FCSTD DOCUMENT  (FreeCAD 1.0R39109 (Git))
Label: 05_assembly_u_1-3
License: All rights reserved
LicenseURL: http://en.wikipedia.org/wiki/All_rights_reserved
objects: App::Link×60, App::FeaturePython×28, Assembly::AssemblyLink×10, TechDraw::DrawProjGroupItem×2, Spreadsheet::Sheet×1, TechDraw::DrawSVGTemplate×1, Assembly::JointGroup×1, Assembly::AssemblyObject×1, TechDraw::DrawProjGroup×1, TechDraw::DrawViewDimension×1, TechDraw::DrawPage×1
note: 2 computed .brp shape members not serialized (recipe doc carries the construction recipe); baked Part::Feature solids carry a one-line shape summary decoded from their .brp
EXTERNAL_REF file=10_assembly_u-shape.FCStd obj=Assembly
EXTERNAL_REF file=11_foot.FCStd obj=Body
EXTERNAL_REF file=12_cross_beam.FCStd obj=Body
EXTERNAL_REF file=10_assembly_u-shape.FCStd obj=Body
EXTERNAL_REF file=10_assembly_u-shape.FCStd obj=Body001
EXTERNAL_REF file=10_assembly_u-shape.FCStd obj=Body002

FEATURE [App::Link] Body
  LinkedObject = -> <external 11_foot.FCStd>#Body
FEATURE [App::Link] Body001
  LinkPlacement = pos=(-1.033e-13,1034,2.296e-13) rot=(0,0,1;3.14159rad)
  LinkedObject = -> <external 11_foot.FCStd>#Body
  Placement = pos=(-1.033e-13,1034,2.296e-13) rot=(0,0,1;3.14159rad)
FEATURE [App::Link] Body002
  LinkPlacement = pos=(-1.129e-13,-18,18) rot=(-1,0,0;1.5708rad)
  LinkedObject = -> <external 12_cross_beam.FCStd>#Body
  Placement = pos=(-1.129e-13,-18,18) rot=(-1,0,0;1.5708rad)
FEATURE [App::Link] Body003
  LinkedObject = -> <external 11_foot.FCStd>#Body
FEATURE [App::Link] Body004
  LinkPlacement = pos=(-1.033e-13,1034,2.296e-13) rot=(0,0,1;3.14159rad)
  LinkedObject = -> <external 11_foot.FCStd>#Body
  Placement = pos=(-1.033e-13,1034,2.296e-13) rot=(0,0,1;3.14159rad)
FEATURE [App::Link] Body005
  LinkPlacement = pos=(-1.129e-13,-18,18) rot=(-1,0,0;1.5708rad)
  LinkedObject = -> <external 12_cross_beam.FCStd>#Body
  Placement = pos=(-1.129e-13,-18,18) rot=(-1,0,0;1.5708rad)
FEATURE [Spreadsheet::Sheet] Spreadsheet
  cells = A2='Distanz; B2(distance)=36
FEATURE [App::FeaturePython] Joint  label="Distance"  # Assembly joint (typed FeaturePython)
  Activated = true
  AngleMax = 0
  AngleMin = 0
  Detach1 = false
  Detach2 = false
  Distance = 0
  Distance2 = 0
  EnableAngleMax = false
  EnableAngleMin = false
  EnableLengthMax = false
  EnableLengthMin = false
  JointType = 5 (Distance)
  LengthMax = 0
  LengthMin = 0
  Placement1 = pos=(3.8e-15,-17,122.081) rot=(1,0,0;4.71239rad)
  Placement2 = pos=(3.8e-15,-17,122.081) rot=(1,0,0;4.71239rad)
  Reference1 = -> Assembly [Assembly001.Body001.Face3,Assembly001.Body001.Vertex13]
  Reference2 = -> Assembly [Assembly002.Body004.Face3,Assembly002.Body004.Vertex12]
FEATURE [App::FeaturePython] Joint001  label="Distance001"  # Assembly joint (typed FeaturePython)
  Activated = true
  AngleMax = 0
  AngleMin = 0
  Detach1 = false
  Detach2 = false
  Distance = 0
  Distance2 = 0
  EnableAngleMax = false
  EnableAngleMin = false
  EnableLengthMax = false
  EnableLengthMin = false
  JointType = 5 (Distance)
  LengthMax = 0
  LengthMin = 0
  Placement1 = pos=(-1e-15,17,535) rot=(0,-0.707107,0.707107;3.14159rad)
  Placement2 = pos=(-1e-15,17,535) rot=(0,-0.707107,0.707107;3.14159rad)
  Reference1 = -> Assembly [Assembly001.Body002.Face5,Assembly001.Body002.Vertex23]
  Reference2 = -> Assembly [Assembly002.Body005.Face5,Assembly002.Body005.Vertex23]
FEATURE [App::FeaturePython] Joint002  label="Distance002"  # Assembly joint (typed FeaturePython)
  Activated = true
  AngleMax = 0
  AngleMin = 0
  Detach1 = false
  Detach2 = false
  Distance = -36
  Distance2 = 0
  EnableAngleMax = false
  EnableAngleMin = false
  EnableLengthMax = false
  EnableLengthMin = false
  JointType = 5 (Distance)
  LengthMax = 0
  LengthMin = 0
  Placement1 = pos=(-17,0,117.5) rot=(-0.57735,0.57735,-0.57735;2.0944rad)
  Placement2 = pos=(17,0,117.5) rot=(0.57735,0.57735,-0.57735;4.18879rad)
  Reference1 = -> Assembly [Assembly001.Body001.Face1,Assembly001.Body001.Face1]
  Reference2 = -> Assembly [Assembly002.Body004.Face10,Assembly002.Body004.Vertex5]
  expr: Distance = -Spreadsheet.distance
FEATURE [App::Link] Body006
  LinkedObject = -> <external 11_foot.FCStd>#Body
FEATURE [App::Link] Body007
  LinkPlacement = pos=(-1.033e-13,1034,2.296e-13) rot=(0,0,1;3.14159rad)
  LinkedObject = -> <external 11_foot.FCStd>#Body
  Placement = pos=(-1.033e-13,1034,2.296e-13) rot=(0,0,1;3.14159rad)
FEATURE [App::Link] Body008
  LinkPlacement = pos=(-1.129e-13,-18,18) rot=(-1,0,0;1.5708rad)
  LinkedObject = -> <external 12_cross_beam.FCStd>#Body
  Placement = pos=(-1.129e-13,-18,18) rot=(-1,0,0;1.5708rad)
FEATURE [App::FeaturePython] Joint003  label="Distance003"  # Assembly joint (typed FeaturePython)
  Activated = true
  AngleMax = 0
  AngleMin = 0
  Detach1 = false
  Detach2 = false
  Distance = 0
  Distance2 = 0
  EnableAngleMax = false
  EnableAngleMin = false
  EnableLengthMax = false
  EnableLengthMin = false
  JointType = 5 (Distance)
  LengthMax = 0
  LengthMin = 0
  Placement1 = pos=(3.8e-15,-17,122.081) rot=(1,0,0;4.71239rad)
  Placement2 = pos=(3.8e-15,-17,122.081) rot=(1,0,0;4.71239rad)
  Reference1 = -> Assembly [Assembly003.Body007.Face3,Assembly003.Body007.Vertex12]
  Reference2 = -> Assembly [Assembly002.Body004.Face3,Assembly002.Body004.Vertex13]
FEATURE [App::FeaturePython] Joint004  label="Distance004"  # Assembly joint (typed FeaturePython)
  Activated = true
  AngleMax = 0
  AngleMin = 0
  Detach1 = false
  Detach2 = false
  Distance = 0
  Distance2 = 0
  EnableAngleMax = false
  EnableAngleMin = false
  EnableLengthMax = false
  EnableLengthMin = false
  JointType = 5 (Distance)
  LengthMax = 0
  LengthMin = 0
  Placement1 = pos=(-1e-15,17,535) rot=(0,-0.707107,0.707107;3.14159rad)
  Placement2 = pos=(-1e-15,17,535) rot=(0,-0.707107,0.707107;3.14159rad)
  Reference1 = -> Assembly [Assembly002.Body005.Face5,Assembly002.Body005.Face5]
  Reference2 = -> Assembly [Assembly003.Body008.Face5,Assembly003.Body008.Face5]
FEATURE [App::FeaturePython] Joint005  label="Distance005"  # Assembly joint (typed FeaturePython)
  Activated = true
  AngleMax = 0
  AngleMin = 0
  Detach1 = false
  Detach2 = false
  Distance = -36
  Distance2 = 0
  EnableAngleMax = false
  EnableAngleMin = false
  EnableLengthMax = false
  EnableLengthMin = false
  JointType = 5 (Distance)
  LengthMax = 0
  LengthMin = 0
  Placement1 = pos=(-17,0,117.5) rot=(-0.57735,0.57735,-0.57735;2.0944rad)
  Placement2 = pos=(17,0,117.5) rot=(0.57735,0.57735,-0.57735;4.18879rad)
  Reference1 = -> Assembly [Assembly002.Body004.Face1,Assembly002.Body004.Vertex3]
  Reference2 = -> Assembly [Assembly003.Body007.Face10,Assembly003.Body007.Face10]
  expr: Distance = -Spreadsheet.distance
FEATURE [App::Link] Body009
  LinkedObject = -> <external 11_foot.FCStd>#Body
FEATURE [App::Link] Body010
  LinkPlacement = pos=(-1.033e-13,1034,2.296e-13) rot=(0,0,1;3.14159rad)
  LinkedObject = -> <external 11_foot.FCStd>#Body
  Placement = pos=(-1.033e-13,1034,2.296e-13) rot=(0,0,1;3.14159rad)
FEATURE [App::Link] Body011
  LinkPlacement = pos=(-1.129e-13,-18,18) rot=(-1,0,0;1.5708rad)
  LinkedObject = -> <external 12_cross_beam.FCStd>#Body
  Placement = pos=(-1.129e-13,-18,18) rot=(-1,0,0;1.5708rad)
FEATURE [App::Link] Body012
  LinkedObject = -> <external 11_foot.FCStd>#Body
FEATURE [App::Link] Body013
  LinkPlacement = pos=(-1.033e-13,1034,2.296e-13) rot=(0,0,1;3.14159rad)
  LinkedObject = -> <external 11_foot.FCStd>#Body
  Placement = pos=(-1.033e-13,1034,2.296e-13) rot=(0,0,1;3.14159rad)
FEATURE [App::Link] Body014
  LinkPlacement = pos=(-1.129e-13,-18,18) rot=(-1,0,0;1.5708rad)
  LinkedObject = -> <external 12_cross_beam.FCStd>#Body
  Placement = pos=(-1.129e-13,-18,18) rot=(-1,0,0;1.5708rad)
FEATURE [App::Link] Body015
  LinkedObject = -> <external 11_foot.FCStd>#Body
FEATURE [App::Link] Body016
  LinkPlacement = pos=(-1.033e-13,1034,2.296e-13) rot=(0,0,1;3.14159rad)
  LinkedObject = -> <external 11_foot.FCStd>#Body
  Placement = pos=(-1.033e-13,1034,2.296e-13) rot=(0,0,1;3.14159rad)
FEATURE [App::Link] Body017
  LinkPlacement = pos=(-1.129e-13,-18,18) rot=(-1,0,0;1.5708rad)
  LinkedObject = -> <external 12_cross_beam.FCStd>#Body
  Placement = pos=(-1.129e-13,-18,18) rot=(-1,0,0;1.5708rad)
FEATURE [App::Link] Body018
  LinkedObject = -> <external 11_foot.FCStd>#Body
FEATURE [App::Link] Body019
  LinkPlacement = pos=(-1.033e-13,1034,2.296e-13) rot=(0,0,1;3.14159rad)
  LinkedObject = -> <external 11_foot.FCStd>#Body
  Placement = pos=(-1.033e-13,1034,2.296e-13) rot=(0,0,1;3.14159rad)
FEATURE [App::Link] Body020
  LinkPlacement = pos=(-1.129e-13,-18,18) rot=(-1,0,0;1.5708rad)
  LinkedObject = -> <external 12_cross_beam.FCStd>#Body
  Placement = pos=(-1.129e-13,-18,18) rot=(-1,0,0;1.5708rad)
FEATURE [App::FeaturePython] Joint006  label="Distance006"  # Assembly joint (typed FeaturePython)
  Activated = true
  AngleMax = 0
  AngleMin = 0
  Detach1 = false
  Detach2 = false
  Distance = 0
  Distance2 = 0
  EnableAngleMax = false
  EnableAngleMin = false
  EnableLengthMax = false
  EnableLengthMin = false
  JointType = 5 (Distance)
  LengthMax = 0
  LengthMin = 0
  Placement1 = pos=(3.8e-15,-17,122.081) rot=(1,0,0;4.71239rad)
  Placement2 = pos=(3.8e-15,-17,122.081) rot=(1,0,0;4.71239rad)
  Reference1 = -> Assembly [Assembly004.Body010.Face3,Assembly004.Body010.Vertex12]
  Reference2 = -> Assembly [Assembly003.Body007.Face3,Assembly003.Body007.Face3]
FEATURE [App::FeaturePython] Joint007  label="Distance007"  # Assembly joint (typed FeaturePython)
  Activated = true
  AngleMax = 0
  AngleMin = 0
  Detach1 = false
  Detach2 = false
  Distance = 0
  Distance2 = 0
  EnableAngleMax = false
  EnableAngleMin = false
  EnableLengthMax = false
  EnableLengthMin = false
  JointType = 5 (Distance)
  LengthMax = 0
  LengthMin = 0
  Placement1 = pos=(-1e-15,17,535) rot=(0,-0.707107,0.707107;3.14159rad)
  Placement2 = pos=(-1e-15,17,535) rot=(0,-0.707107,0.707107;3.14159rad)
  Reference1 = -> Assembly [Assembly004.Body011.Face5,Assembly004.Body011.Vertex23]
  Reference2 = -> Assembly [Assembly003.Body008.Face5,Assembly003.Body008.Vertex4]
FEATURE [App::FeaturePython] Joint008  label="Distance008"  # Assembly joint (typed FeaturePython)
  Activated = true
  AngleMax = 0
  AngleMin = 0
  Detach1 = false
  Detach2 = false
  Distance = -36
  Distance2 = 0
  EnableAngleMax = false
  EnableAngleMin = false
  EnableLengthMax = false
  EnableLengthMin = false
  JointType = 5 (Distance)
  LengthMax = 0
  LengthMin = 0
  Placement1 = pos=(-17,0,117.5) rot=(-0.57735,0.57735,-0.57735;2.0944rad)
  Placement2 = pos=(17,0,117.5) rot=(0.57735,0.57735,-0.57735;4.18879rad)
  Reference1 = -> Assembly [Assembly003.Body007.Face1,Assembly003.Body007.Vertex3]
  Reference2 = -> Assembly [Assembly004.Body010.Face10,Assembly004.Body010.Vertex5]
  expr: Distance = -<<Spreadsheet>>.distance
FEATURE [App::FeaturePython] Joint009  label="Distance009"  # Assembly joint (typed FeaturePython)
  Activated = true
  AngleMax = 0
  AngleMin = 0
  Detach1 = false
  Detach2 = false
  Distance = 0
  Distance2 = 0
  EnableAngleMax = false
  EnableAngleMin = false
  EnableLengthMax = false
  EnableLengthMin = false
  JointType = 5 (Distance)
  LengthMax = 0
  LengthMin = 0
  Placement1 = pos=(3.8e-15,-17,122.081) rot=(1,0,0;4.71239rad)
  Placement2 = pos=(3.8e-15,-17,122.081) rot=(1,0,0;4.71239rad)
  Reference1 = -> Assembly [Assembly005.Body013.Face3,Assembly005.Body013.Vertex12]
  Reference2 = -> Assembly [Assembly004.Body010.Face3,Assembly004.Body010.Vertex13]
FEATURE [App::FeaturePython] Joint010  label="Distance010"  # Assembly joint (typed FeaturePython)
  Activated = true
  AngleMax = 0
  AngleMin = 0
  Detach1 = false
  Detach2 = false
  Distance = 0
  Distance2 = 0
  EnableAngleMax = false
  EnableAngleMin = false
  EnableLengthMax = false
  EnableLengthMin = false
  JointType = 5 (Distance)
  LengthMax = 0
  LengthMin = 0
  Placement1 = pos=(-1e-15,17,535) rot=(0,-0.707107,0.707107;3.14159rad)
  Placement2 = pos=(-1e-15,17,535) rot=(0,-0.707107,0.707107;3.14159rad)
  Reference1 = -> Assembly [Assembly005.Body014.Face5,Assembly005.Body014.Vertex16]
  Reference2 = -> Assembly [Assembly004.Body011.Face5,Assembly004.Body011.Face5]
FEATURE [App::FeaturePython] Joint011  label="Distance011"  # Assembly joint (typed FeaturePython)
  Activated = true
  AngleMax = 0
  AngleMin = 0
  Detach1 = false
  Detach2 = false
  Distance = -36
  Distance2 = 0
  EnableAngleMax = false
  EnableAngleMin = false
  EnableLengthMax = false
  EnableLengthMin = false
  JointType = 5 (Distance)
  LengthMax = 0
  LengthMin = 0
  Placement1 = pos=(-17,0,117.5) rot=(-0.57735,0.57735,-0.57735;2.0944rad)
  Placement2 = pos=(17,0,117.5) rot=(0.57735,0.57735,-0.57735;4.18879rad)
  Reference1 = -> Assembly [Assembly004.Body010.Face1,Assembly004.Body010.Face1]
  Reference2 = -> Assembly [Assembly005.Body013.Face10,Assembly005.Body013.Vertex5]
  expr: Distance = -Spreadsheet.distance
FEATURE [App::FeaturePython] Joint012  label="Distance012"  # Assembly joint (typed FeaturePython)
  Activated = true
  AngleMax = 0
  AngleMin = 0
  Detach1 = false
  Detach2 = false
  Distance = 0
  Distance2 = 0
  EnableAngleMax = false
  EnableAngleMin = false
  EnableLengthMax = false
  EnableLengthMin = false
  JointType = 5 (Distance)
  LengthMax = 0
  LengthMin = 0
  Placement1 = pos=(3.8e-15,-17,122.081) rot=(1,0,0;4.71239rad)
  Placement2 = pos=(3.8e-15,-17,122.081) rot=(1,0,0;4.71239rad)
  Reference1 = -> Assembly [Assembly005.Body013.Face3,Assembly005.Body013.Face3]
  Reference2 = -> Assembly [Assembly006.Body016.Face3,Assembly006.Body016.Vertex13]
FEATURE [App::FeaturePython] Joint013  label="Distance013"  # Assembly joint (typed FeaturePython)
  Activated = true
  AngleMax = 0
  AngleMin = 0
  Detach1 = false
  Detach2 = false
  Distance = 0
  Distance2 = 0
  EnableAngleMax = false
  EnableAngleMin = false
  EnableLengthMax = false
  EnableLengthMin = false
  JointType = 5 (Distance)
  LengthMax = 0
  LengthMin = 0
  Placement1 = pos=(-1e-15,17,535) rot=(0,-0.707107,0.707107;3.14159rad)
  Placement2 = pos=(-1e-15,17,535) rot=(0,-0.707107,0.707107;3.14159rad)
  Reference1 = -> Assembly [Assembly006.Body017.Face5,Assembly006.Body017.Vertex23]
  Reference2 = -> Assembly [Assembly005.Body014.Face5,Assembly005.Body014.Vertex16]
FEATURE [App::FeaturePython] Joint014  label="Distance014"  # Assembly joint (typed FeaturePython)
  Activated = true
  AngleMax = 0
  AngleMin = 0
  Detach1 = false
  Detach2 = false
  Distance = -36
  Distance2 = 0
  EnableAngleMax = false
  EnableAngleMin = false
  EnableLengthMax = false
  EnableLengthMin = false
  JointType = 5 (Distance)
  LengthMax = 0
  LengthMin = 0
  Placement1 = pos=(17,0,117.5) rot=(0.57735,0.57735,-0.57735;4.18879rad)
  Placement2 = pos=(-17,0,117.5) rot=(-0.57735,0.57735,-0.57735;2.0944rad)
  Reference1 = -> Assembly [Assembly006.Body016.Face10,Assembly006.Body016.Vertex5]
  Reference2 = -> Assembly [Assembly005.Body013.Face1,Assembly005.Body013.Face1]
  expr: Distance = -Spreadsheet.distance
FEATURE [App::FeaturePython] Joint015  label="Distance015"  # Assembly joint (typed FeaturePython)
  Activated = true
  AngleMax = 0
  AngleMin = 0
  Detach1 = false
  Detach2 = false
  Distance = 0
  Distance2 = 0
  EnableAngleMax = false
  EnableAngleMin = false
  EnableLengthMax = false
  EnableLengthMin = false
  JointType = 5 (Distance)
  LengthMax = 0
  LengthMin = 0
  Placement1 = pos=(3.8e-15,-17,122.081) rot=(1,0,0;4.71239rad)
  Placement2 = pos=(3.8e-15,-17,122.081) rot=(1,0,0;4.71239rad)
  Reference1 = -> Assembly [Assembly007.Body019.Face3,Assembly007.Body019.Vertex12]
  Reference2 = -> Assembly [Assembly006.Body016.Face3,Assembly006.Body016.Face3]
FEATURE [App::FeaturePython] Joint016  label="Distance016"  # Assembly joint (typed FeaturePython)
  Activated = true
  AngleMax = 0
  AngleMin = 0
  Detach1 = false
  Detach2 = false
  Distance = 0
  Distance2 = 0
  EnableAngleMax = false
  EnableAngleMin = false
  EnableLengthMax = false
  EnableLengthMin = false
  JointType = 5 (Distance)
  LengthMax = 0
  LengthMin = 0
  Placement1 = pos=(-1e-15,17,535) rot=(0,-0.707107,0.707107;3.14159rad)
  Placement2 = pos=(-1e-15,17,535) rot=(0,-0.707107,0.707107;3.14159rad)
  Reference1 = -> Assembly [Assembly006.Body017.Face5,Assembly006.Body017.Vertex16]
  Reference2 = -> Assembly [Assembly007.Body020.Face5,Assembly007.Body020.Vertex16]
FEATURE [App::FeaturePython] Joint017  label="Distance017"  # Assembly joint (typed FeaturePython)
  Activated = true
  AngleMax = 0
  AngleMin = 0
  Detach1 = false
  Detach2 = false
  Distance = -36
  Distance2 = 0
  EnableAngleMax = false
  EnableAngleMin = false
  EnableLengthMax = false
  EnableLengthMin = false
  JointType = 5 (Distance)
  LengthMax = 0
  LengthMin = 0
  Placement1 = pos=(-17,0,117.5) rot=(-0.57735,0.57735,-0.57735;2.0944rad)
  Placement2 = pos=(17,0,117.5) rot=(0.57735,0.57735,-0.57735;4.18879rad)
  Reference1 = -> Assembly [Assembly006.Body016.Face1,Assembly006.Body016.Vertex1]
  Reference2 = -> Assembly [Assembly007.Body019.Face10,Assembly007.Body019.Vertex15]
  expr: Distance = -Spreadsheet.distance
FEATURE [TechDraw::DrawSVGTemplate] Template
  EditableTexts = approval_person=B. Hecate; creator=A. Nemesis; date_of_issue=22/06/2025; document_type=Assembly Drawing; general_tolerances=ISO 2768-m; identification_number=DN; language_code=EN; part_material=Stainless steel Mat.No. 1.4301; revision_index=AAA; sheet_number=1 / 1; sheet_scale=1 : 1; title=00_assembly_complete_large_x1
  Height = 297
  Orientation = 1
  Template = C:/Program Files/FreeCAD 1.0/data/Mod/TechDraw/Templates/A3_Landscape_ISO5457_minimal.svg
  Width = 420
FEATURE [App::Link] Body021
  LinkedObject = -> <external 11_foot.FCStd>#Body
FEATURE [App::Link] Body022
  LinkPlacement = pos=(-1.033e-13,1034,2.296e-13) rot=(0,0,1;3.14159rad)
  LinkedObject = -> <external 11_foot.FCStd>#Body
  Placement = pos=(-1.033e-13,1034,2.296e-13) rot=(0,0,1;3.14159rad)
FEATURE [App::Link] Body023
  LinkPlacement = pos=(-1.129e-13,-18,18) rot=(-1,0,0;1.5708rad)
  LinkedObject = -> <external 12_cross_beam.FCStd>#Body
  Placement = pos=(-1.129e-13,-18,18) rot=(-1,0,0;1.5708rad)
FEATURE [App::Link] Body024
  LinkedObject = -> <external 11_foot.FCStd>#Body
FEATURE [App::Link] Body025
  LinkPlacement = pos=(-1.033e-13,1034,2.296e-13) rot=(0,0,1;3.14159rad)
  LinkedObject = -> <external 11_foot.FCStd>#Body
  Placement = pos=(-1.033e-13,1034,2.296e-13) rot=(0,0,1;3.14159rad)
FEATURE [App::Link] Body026
  LinkPlacement = pos=(-1.129e-13,-18,18) rot=(-1,0,0;1.5708rad)
  LinkedObject = -> <external 12_cross_beam.FCStd>#Body
  Placement = pos=(-1.129e-13,-18,18) rot=(-1,0,0;1.5708rad)
FEATURE [App::Link] Body027
  LinkedObject = -> <external 11_foot.FCStd>#Body
FEATURE [App::Link] Body028
  LinkPlacement = pos=(-1.033e-13,1034,2.296e-13) rot=(0,0,1;3.14159rad)
  LinkedObject = -> <external 11_foot.FCStd>#Body
  Placement = pos=(-1.033e-13,1034,2.296e-13) rot=(0,0,1;3.14159rad)
FEATURE [App::Link] Body029
  LinkPlacement = pos=(-1.129e-13,-18,18) rot=(-1,0,0;1.5708rad)
  LinkedObject = -> <external 12_cross_beam.FCStd>#Body
  Placement = pos=(-1.129e-13,-18,18) rot=(-1,0,0;1.5708rad)
FEATURE [App::FeaturePython] Joint018  label="Distance018"  # Assembly joint (typed FeaturePython)
  Activated = true
  AngleMax = 0
  AngleMin = 0
  Detach1 = false
  Detach2 = false
  Distance = 0
  Distance2 = 0
  EnableAngleMax = false
  EnableAngleMin = false
  EnableLengthMax = false
  EnableLengthMin = false
  JointType = 5 (Distance)
  LengthMax = 0
  LengthMin = 0
  Placement1 = pos=(-1e-15,17,535) rot=(0,-0.707107,0.707107;3.14159rad)
  Placement2 = pos=(-1e-15,17,535) rot=(0,-0.707107,0.707107;3.14159rad)
  Reference1 = -> Assembly [Assembly007.Body020.Face5,Assembly007.Body020.Vertex23]
  Reference2 = -> Assembly [Assembly008.Body023.Face5,Assembly008.Body023.Vertex16]
FEATURE [App::FeaturePython] Joint019  label="Distance019"  # Assembly joint (typed FeaturePython)
  Activated = true
  AngleMax = 0
  AngleMin = 0
  Detach1 = false
  Detach2 = false
  Distance = 0
  Distance2 = 0
  EnableAngleMax = false
  EnableAngleMin = false
  EnableLengthMax = false
  EnableLengthMin = false
  JointType = 5 (Distance)
  LengthMax = 0
  LengthMin = 0
  Placement1 = pos=(3.8e-15,-17,122.081) rot=(1,0,0;4.71239rad)
  Placement2 = pos=(3.8e-15,-17,122.081) rot=(1,0,0;4.71239rad)
  Reference1 = -> Assembly [Assembly008.Body022.Face3,Assembly008.Body022.Face3]
  Reference2 = -> Assembly [Assembly007.Body019.Face3,Assembly007.Body019.Vertex13]
FEATURE [App::FeaturePython] Joint020  label="Distance020"  # Assembly joint (typed FeaturePython)
  Activated = true
  AngleMax = 0
  AngleMin = 0
  Detach1 = false
  Detach2 = false
  Distance = -36
  Distance2 = 0
  EnableAngleMax = false
  EnableAngleMin = false
  EnableLengthMax = false
  EnableLengthMin = false
  JointType = 5 (Distance)
  LengthMax = 0
  LengthMin = 0
  Placement1 = pos=(-17,0,117.5) rot=(-0.57735,0.57735,-0.57735;2.0944rad)
  Placement2 = pos=(17,0,117.5) rot=(0.57735,0.57735,-0.57735;4.18879rad)
  Reference1 = -> Assembly [Assembly007.Body019.Face1,Assembly007.Body019.Face1]
  Reference2 = -> Assembly [Assembly008.Body022.Face10,Assembly008.Body022.Vertex5]
  expr: Distance = -Spreadsheet.distance
FEATURE [App::FeaturePython] Joint021  label="Distance021"  # Assembly joint (typed FeaturePython)
  Activated = true
  AngleMax = 0
  AngleMin = 0
  Detach1 = false
  Detach2 = false
  Distance = 0
  Distance2 = 0
  EnableAngleMax = false
  EnableAngleMin = false
  EnableLengthMax = false
  EnableLengthMin = false
  JointType = 5 (Distance)
  LengthMax = 0
  LengthMin = 0
  Placement1 = pos=(3.8e-15,-17,122.081) rot=(1,0,0;4.71239rad)
  Placement2 = pos=(3.8e-15,-17,122.081) rot=(1,0,0;4.71239rad)
  Reference1 = -> Assembly [Assembly009.Body025.Face3,Assembly009.Body025.Vertex13]
  Reference2 = -> Assembly [Assembly008.Body022.Face3,Assembly008.Body022.Vertex13]
FEATURE [App::FeaturePython] Joint022  label="Distance022"  # Assembly joint (typed FeaturePython)
  Activated = true
  AngleMax = 0
  AngleMin = 0
  Detach1 = false
  Detach2 = false
  Distance = 0
  Distance2 = 0
  EnableAngleMax = false
  EnableAngleMin = false
  EnableLengthMax = false
  EnableLengthMin = false
  JointType = 5 (Distance)
  LengthMax = 0
  LengthMin = 0
  Placement1 = pos=(-1e-15,17,535) rot=(0,-0.707107,0.707107;3.14159rad)
  Placement2 = pos=(-1e-15,17,535) rot=(0,-0.707107,0.707107;3.14159rad)
  Reference1 = -> Assembly [Assembly009.Body026.Face5,Assembly009.Body026.Face5]
  Reference2 = -> Assembly [Assembly008.Body023.Face5,Assembly008.Body023.Face5]
FEATURE [App::FeaturePython] Joint023  label="Distance023"  # Assembly joint (typed FeaturePython)
  Activated = true
  AngleMax = 0
  AngleMin = 0
  Detach1 = false
  Detach2 = false
  Distance = -36
  Distance2 = 0
  EnableAngleMax = false
  EnableAngleMin = false
  EnableLengthMax = false
  EnableLengthMin = false
  JointType = 5 (Distance)
  LengthMax = 0
  LengthMin = 0
  Placement1 = pos=(-17,0,117.5) rot=(-0.57735,0.57735,-0.57735;2.0944rad)
  Placement2 = pos=(17,0,117.5) rot=(0.57735,0.57735,-0.57735;4.18879rad)
  Reference1 = -> Assembly [Assembly008.Body022.Face1,Assembly008.Body022.Face1]
  Reference2 = -> Assembly [Assembly009.Body025.Face10,Assembly009.Body025.Vertex5]
  expr: Distance = -Spreadsheet.distance
FEATURE [App::FeaturePython] Joint024  label="Distance024"  # Assembly joint (typed FeaturePython)
  Activated = true
  AngleMax = 0
  AngleMin = 0
  Detach1 = false
  Detach2 = false
  Distance = 0
  Distance2 = 0
  EnableAngleMax = false
  EnableAngleMin = false
  EnableLengthMax = false
  EnableLengthMin = false
  JointType = 5 (Distance)
  LengthMax = 0
  LengthMin = 0
  Placement1 = pos=(3.8e-15,-17,122.081) rot=(1,0,0;4.71239rad)
  Placement2 = pos=(3.8e-15,-17,122.081) rot=(1,0,0;4.71239rad)
  Reference1 = -> Assembly [Assembly009.Body025.Face3,Assembly009.Body025.Vertex12]
  Reference2 = -> Assembly [Assembly010.Body028.Face3,Assembly010.Body028.Face3]
FEATURE [App::FeaturePython] Joint025  label="Distance025"  # Assembly joint (typed FeaturePython)
  Activated = true
  AngleMax = 0
  AngleMin = 0
  Detach1 = false
  Detach2 = false
  Distance = 0
  Distance2 = 0
  EnableAngleMax = false
  EnableAngleMin = false
  EnableLengthMax = false
  EnableLengthMin = false
  JointType = 5 (Distance)
  LengthMax = 0
  LengthMin = 0
  Placement1 = pos=(-1e-15,17,535) rot=(0,-0.707107,0.707107;3.14159rad)
  Placement2 = pos=(-1e-15,17,535) rot=(0,-0.707107,0.707107;3.14159rad)
  Reference1 = -> Assembly [Assembly010.Body029.Face5,Assembly010.Body029.Vertex23]
  Reference2 = -> Assembly [Assembly009.Body026.Face5,Assembly009.Body026.Vertex16]
FEATURE [App::FeaturePython] Joint026  label="Distance026"  # Assembly joint (typed FeaturePython)
  Activated = true
  AngleMax = 0
  AngleMin = 0
  Detach1 = false
  Detach2 = false
  Distance = -36
  Distance2 = 0
  EnableAngleMax = false
  EnableAngleMin = false
  EnableLengthMax = false
  EnableLengthMin = false
  JointType = 5 (Distance)
  LengthMax = 0
  LengthMin = 0
  Placement1 = pos=(-17,0,117.5) rot=(-0.57735,0.57735,-0.57735;2.0944rad)
  Placement2 = pos=(17,-17,117.5) rot=(0,0,1;0rad)
  Reference1 = -> Assembly [Assembly009.Body025.Face1,Assembly009.Body025.Face1]
  Reference2 = -> Assembly [Assembly010.Body028.Edge17,Assembly010.Body028.Vertex15]
  expr: Distance = -Spreadsheet.distance
FEATURE [App::Link] Body030
  LinkedObject = -> <external 10_assembly_u-shape.FCStd>#Body
FEATURE [App::Link] Body031
  LinkPlacement = pos=(1.87e-14,1034,-3.446e-13) rot=(0,0,1;3.14159rad)
  LinkedObject = -> <external 10_assembly_u-shape.FCStd>#Body001
  Placement = pos=(1.87e-14,1034,-3.446e-13) rot=(0,0,1;3.14159rad)
FEATURE [App::Link] Body032
  LinkPlacement = pos=(-2.8e-15,-18,18) rot=(1,0,0;4.71239rad)
  LinkedObject = -> <external 10_assembly_u-shape.FCStd>#Body002
  Placement = pos=(-2.8e-15,-18,18) rot=(1,0,0;4.71239rad)
FEATURE [Assembly::AssemblyLink] Assembly001
  Group = -> [Body,Body001,Body002,Body030,Body031,Body032]
  LinkedObject = -> <external 10_assembly_u-shape.FCStd>#Assembly
  Origin = -> Origin001
  Rigid = true
FEATURE [App::FeaturePython] GroundedJoint  # Assembly grounded joint (typed FeaturePython)
  ObjectToGround = -> Assembly001
FEATURE [Assembly::JointGroup] Joints
  Group = -> [GroundedJoint,Joint,Joint001,Joint002,Joint003,Joint004,Joint005,Joint006,Joint007,Joint008,Joint009,Joint010,Joint011,Joint012,Joint013,Joint014,Joint015,Joint016,Joint017,Joint018,Joint019,Joint020,Joint021,Joint022,Joint023,Joint024,Joint025,Joint026]
FEATURE [App::Link] Body033
  LinkedObject = -> <external 10_assembly_u-shape.FCStd>#Body
FEATURE [App::Link] Body034
  LinkPlacement = pos=(1.87e-14,1034,-3.446e-13) rot=(0,0,1;3.14159rad)
  LinkedObject = -> <external 10_assembly_u-shape.FCStd>#Body001
  Placement = pos=(1.87e-14,1034,-3.446e-13) rot=(0,0,1;3.14159rad)
FEATURE [App::Link] Body035
  LinkPlacement = pos=(-2.8e-15,-18,18) rot=(1,0,0;4.71239rad)
  LinkedObject = -> <external 10_assembly_u-shape.FCStd>#Body002
  Placement = pos=(-2.8e-15,-18,18) rot=(1,0,0;4.71239rad)
FEATURE [Assembly::AssemblyLink] Assembly002
  Group = -> [Body003,Body004,Body005,Body033,Body034,Body035]
  LinkedObject = -> <external 10_assembly_u-shape.FCStd>#Assembly
  Origin = -> Origin002
  Placement = pos=(70,9.23e-14,-1.3e-15) rot=(0,0,1;0rad)
  Rigid = true
FEATURE [App::Link] Body036
  LinkedObject = -> <external 10_assembly_u-shape.FCStd>#Body
FEATURE [App::Link] Body037
  LinkPlacement = pos=(1.87e-14,1034,-3.446e-13) rot=(0,0,1;3.14159rad)
  LinkedObject = -> <external 10_assembly_u-shape.FCStd>#Body001
  Placement = pos=(1.87e-14,1034,-3.446e-13) rot=(0,0,1;3.14159rad)
FEATURE [App::Link] Body038
  LinkPlacement = pos=(-2.8e-15,-18,18) rot=(1,0,0;4.71239rad)
  LinkedObject = -> <external 10_assembly_u-shape.FCStd>#Body002
  Placement = pos=(-2.8e-15,-18,18) rot=(1,0,0;4.71239rad)
FEATURE [Assembly::AssemblyLink] Assembly003
  Group = -> [Body006,Body007,Body008,Body036,Body037,Body038]
  LinkedObject = -> <external 10_assembly_u-shape.FCStd>#Assembly
  Origin = -> Origin003
  Placement = pos=(140,-2.86e-14,2.39e-14) rot=(0,0,1;0rad)
  Rigid = true
FEATURE [App::Link] Body039
  LinkedObject = -> <external 10_assembly_u-shape.FCStd>#Body
FEATURE [App::Link] Body040
  LinkPlacement = pos=(1.87e-14,1034,-3.446e-13) rot=(0,0,1;3.14159rad)
  LinkedObject = -> <external 10_assembly_u-shape.FCStd>#Body001
  Placement = pos=(1.87e-14,1034,-3.446e-13) rot=(0,0,1;3.14159rad)
FEATURE [App::Link] Body041
  LinkPlacement = pos=(-2.8e-15,-18,18) rot=(1,0,0;4.71239rad)
  LinkedObject = -> <external 10_assembly_u-shape.FCStd>#Body002
  Placement = pos=(-2.8e-15,-18,18) rot=(1,0,0;4.71239rad)
FEATURE [Assembly::AssemblyLink] Assembly004
  Group = -> [Body009,Body010,Body011,Body039,Body040,Body041]
  LinkedObject = -> <external 10_assembly_u-shape.FCStd>#Assembly
  Origin = -> Origin004
  Placement = pos=(210,2.578e-13,4.84e-14) rot=(0,0,1;0rad)
  Rigid = true
FEATURE [App::Link] Body042
  LinkedObject = -> <external 10_assembly_u-shape.FCStd>#Body
FEATURE [App::Link] Body043
  LinkPlacement = pos=(1.87e-14,1034,-3.446e-13) rot=(0,0,1;3.14159rad)
  LinkedObject = -> <external 10_assembly_u-shape.FCStd>#Body001
  Placement = pos=(1.87e-14,1034,-3.446e-13) rot=(0,0,1;3.14159rad)
FEATURE [App::Link] Body044
  LinkPlacement = pos=(-2.8e-15,-18,18) rot=(1,0,0;4.71239rad)
  LinkedObject = -> <external 10_assembly_u-shape.FCStd>#Body002
  Placement = pos=(-2.8e-15,-18,18) rot=(1,0,0;4.71239rad)
FEATURE [Assembly::AssemblyLink] Assembly005
  Group = -> [Body012,Body013,Body014,Body042,Body043,Body044]
  LinkedObject = -> <external 10_assembly_u-shape.FCStd>#Assembly
  Origin = -> Origin005
  Placement = pos=(280,1.496e-13,1.001e-13) rot=(0,0,1;0rad)
  Rigid = true
FEATURE [App::Link] Body045
  LinkedObject = -> <external 10_assembly_u-shape.FCStd>#Body
FEATURE [App::Link] Body046
  LinkPlacement = pos=(1.87e-14,1034,-3.446e-13) rot=(0,0,1;3.14159rad)
  LinkedObject = -> <external 10_assembly_u-shape.FCStd>#Body001
  Placement = pos=(1.87e-14,1034,-3.446e-13) rot=(0,0,1;3.14159rad)
FEATURE [App::Link] Body047
  LinkPlacement = pos=(-2.8e-15,-18,18) rot=(1,0,0;4.71239rad)
  LinkedObject = -> <external 10_assembly_u-shape.FCStd>#Body002
  Placement = pos=(-2.8e-15,-18,18) rot=(1,0,0;4.71239rad)
FEATURE [Assembly::AssemblyLink] Assembly006
  Group = -> [Body015,Body016,Body017,Body045,Body046,Body047]
  LinkedObject = -> <external 10_assembly_u-shape.FCStd>#Assembly
  Origin = -> Origin006
  Placement = pos=(350,6.31e-14,1.758e-13) rot=(0,0,1;0rad)
  Rigid = true
FEATURE [App::Link] Body048
  LinkedObject = -> <external 10_assembly_u-shape.FCStd>#Body
FEATURE [App::Link] Body049
  LinkPlacement = pos=(1.87e-14,1034,-3.446e-13) rot=(0,0,1;3.14159rad)
  LinkedObject = -> <external 10_assembly_u-shape.FCStd>#Body001
  Placement = pos=(1.87e-14,1034,-3.446e-13) rot=(0,0,1;3.14159rad)
FEATURE [App::Link] Body050
  LinkPlacement = pos=(-2.8e-15,-18,18) rot=(1,0,0;4.71239rad)
  LinkedObject = -> <external 10_assembly_u-shape.FCStd>#Body002
  Placement = pos=(-2.8e-15,-18,18) rot=(1,0,0;4.71239rad)
FEATURE [Assembly::AssemblyLink] Assembly007
  Group = -> [Body018,Body019,Body020,Body048,Body049,Body050]
  LinkedObject = -> <external 10_assembly_u-shape.FCStd>#Assembly
  Origin = -> Origin007
  Placement = pos=(420,-1.137e-13,2.479e-13) rot=(0,0,1;0rad)
  Rigid = true
FEATURE [App::Link] Body051
  LinkedObject = -> <external 10_assembly_u-shape.FCStd>#Body
FEATURE [App::Link] Body052
  LinkPlacement = pos=(1.87e-14,1034,-3.446e-13) rot=(0,0,1;3.14159rad)
  LinkedObject = -> <external 10_assembly_u-shape.FCStd>#Body001
  Placement = pos=(1.87e-14,1034,-3.446e-13) rot=(0,0,1;3.14159rad)
FEATURE [App::Link] Body053
  LinkPlacement = pos=(-2.8e-15,-18,18) rot=(1,0,0;4.71239rad)
  LinkedObject = -> <external 10_assembly_u-shape.FCStd>#Body002
  Placement = pos=(-2.8e-15,-18,18) rot=(1,0,0;4.71239rad)
FEATURE [Assembly::AssemblyLink] Assembly008
  Group = -> [Body021,Body022,Body023,Body051,Body052,Body053]
  LinkedObject = -> <external 10_assembly_u-shape.FCStd>#Assembly
  Origin = -> Origin008
  Placement = pos=(490,2.783e-13,3.238e-13) rot=(0,0,1;0rad)
  Rigid = true
FEATURE [App::Link] Body054
  LinkedObject = -> <external 10_assembly_u-shape.FCStd>#Body
FEATURE [App::Link] Body055
  LinkPlacement = pos=(1.87e-14,1034,-3.446e-13) rot=(0,0,1;3.14159rad)
  LinkedObject = -> <external 10_assembly_u-shape.FCStd>#Body001
  Placement = pos=(1.87e-14,1034,-3.446e-13) rot=(0,0,1;3.14159rad)
FEATURE [App::Link] Body056
  LinkPlacement = pos=(-2.8e-15,-18,18) rot=(1,0,0;4.71239rad)
  LinkedObject = -> <external 10_assembly_u-shape.FCStd>#Body002
  Placement = pos=(-2.8e-15,-18,18) rot=(1,0,0;4.71239rad)
FEATURE [Assembly::AssemblyLink] Assembly009
  Group = -> [Body024,Body025,Body026,Body054,Body055,Body056]
  LinkedObject = -> <external 10_assembly_u-shape.FCStd>#Assembly
  Origin = -> Origin009
  Placement = pos=(560,4.117e-13,4.196e-13) rot=(0,0,1;0rad)
  Rigid = true
FEATURE [App::Link] Body057
  LinkedObject = -> <external 10_assembly_u-shape.FCStd>#Body
FEATURE [App::Link] Body058
  LinkPlacement = pos=(1.87e-14,1034,-3.446e-13) rot=(0,0,1;3.14159rad)
  LinkedObject = -> <external 10_assembly_u-shape.FCStd>#Body001
  Placement = pos=(1.87e-14,1034,-3.446e-13) rot=(0,0,1;3.14159rad)
FEATURE [App::Link] Body059
  LinkPlacement = pos=(-2.8e-15,-18,18) rot=(1,0,0;4.71239rad)
  LinkedObject = -> <external 10_assembly_u-shape.FCStd>#Body002
  Placement = pos=(-2.8e-15,-18,18) rot=(1,0,0;4.71239rad)
FEATURE [Assembly::AssemblyLink] Assembly010
  Group = -> [Body027,Body028,Body029,Body057,Body058,Body059]
  LinkedObject = -> <external 10_assembly_u-shape.FCStd>#Assembly
  Origin = -> Origin010
  Placement = pos=(630,3.525e-13,5.167e-13) rot=(0,0,1;0rad)
  Rigid = true
FEATURE [Assembly::AssemblyObject] Assembly
  Group = -> [Joints,Assembly001,GroundedJoint,Assembly002,Joint,Joint001,Joint002,Assembly003,Joint003,Joint004,Joint005,Assembly004,Assembly005,Assembly006,Assembly007,Joint006,Joint007,Joint008,Joint009,Joint010,Joint011,Joint012,Joint013,Joint014,Joint015,Joint016,Joint017,Assembly008,Assembly009,Assembly010,Joint018,Joint019,Joint020,Joint021,Joint022,Joint023,Joint024,Joint025,Joint026]
  Origin = -> Origin
  Type = Assembly
FEATURE [TechDraw::DrawProjGroupItem] View  label="Front"
  CoarseView = false
  Direction = (0,-1,0)
  Focus = 100
  HardHidden = false
  IsoCount = 0
  IsoHidden = false
  IsoVisible = false
  LockPosition = true
  Perspective = false
  Rotation = 0
  RotationVector = (1,0,0)
  Scale = 0.2
  ScaleType = 2
  ScrubCount = 1
  SeamHidden = false
  SeamVisible = true
  SmoothHidden = false
  SmoothVisible = true
  Source = -> [Assembly001,Assembly002,Assembly003,Assembly004,Assembly005,Assembly006,Assembly007,Assembly008,Assembly009,Assembly010]
  Type = 0
  X = 0
  XDirection = (-1,0,-1e-16)
  Y = 0
FEATURE [TechDraw::DrawProjGroupItem] ProjItem  label="Left"
  CoarseView = false
  Direction = (1,-1e-16,1e-16)
  Focus = 100
  HardHidden = false
  IsoCount = 0
  IsoHidden = false
  IsoVisible = false
  LockPosition = false
  Perspective = false
  Rotation = 0
  RotationVector = (1,0,0)
  Scale = 0.2
  ScaleType = 2
  ScrubCount = 1
  SeamHidden = false
  SeamVisible = true
  SmoothHidden = false
  SmoothVisible = true
  Source = -> [Assembly001,Assembly002,Assembly003,Assembly004,Assembly005,Assembly006,Assembly007,Assembly008,Assembly009,Assembly010]
  Type = 1
  X = 188.4
  XDirection = (-1e-16,-1,0)
  Y = 0
FEATURE [TechDraw::DrawProjGroup] ProjGroup
  Anchor = -> View
  AutoDistribute = true
  LockPosition = false
  ProjectionType = 0
  Rotation = 0
  Scale = 0.2
  ScaleType = 2
  Source = -> [Assembly001,Assembly002,Assembly003,Assembly004,Assembly005,Assembly006,Assembly007,Assembly008,Assembly009,Assembly010]
  Views = -> [View,ProjItem]
  X = 113.05
  Y = 166.942
  spacingX = 15
  spacingY = 15
FEATURE [TechDraw::DrawViewDimension] Dimension
  AngleOverride = false
  Arbitrary = false
  ArbitraryTolerances = false
  BoxCorners = (2) [(-66.4,-23.5,0),(66.4,23.5,0)]
  EqualTolerance = true
  ExtensionAngle = 0
  FormatSpec = %.2w
  FormatSpecOverTolerance = %+.2w
  FormatSpecUnderTolerance = %+.2w
  Inverted = false
  LineAngle = 0
  LockPosition = false
  MeasureType = 1
  OverTolerance = 0
  References2D = -> [View]
  Rotation = 0
  ScaleType = 0
  TheoreticalExact = false
  Type = 0
  UnderTolerance = 0
  X = 0
  Y = 41.766
FEATURE [TechDraw::DrawPage] Page
  KeepUpdated = true
  NextBalloonIndex = 1
  ProjectionType = 0
  Template = -> Template
  Views = -> [ProjGroup,Dimension]

RESOLVED EXTERNAL PARTS (link-assembly join: the EXTERNAL_REF files above that resolve inside this repo's crawl, each included once):
---- part 10_assembly_u-shape.FCStd = doc fcstd_1a8c6db84407 ----
FCSTD DOCUMENT  (FreeCAD 1.0R39109 (Git))
Label: 10_assembly_u-shape
License: All rights reserved
LicenseURL: http://en.wikipedia.org/wiki/All_rights_reserved
objects: App::FeaturePython×7, App::Link×3, Assembly::JointGroup×1, Assembly::AssemblyObject×1
EXTERNAL_REF file=11_foot.FCStd obj=Body
EXTERNAL_REF file=12_cross_beam.FCStd obj=Body

FEATURE [App::Link] Body
  LinkedObject = -> <external 11_foot.FCStd>#Body
FEATURE [App::FeaturePython] GroundedJoint  # Assembly grounded joint (typed FeaturePython)
  ObjectToGround = -> Body
FEATURE [App::Link] Body001
  LinkPlacement = pos=(1.87e-14,1034,-3.446e-13) rot=(0,0,1;3.14159rad)
  LinkedObject = -> <external 11_foot.FCStd>#Body
  Placement = pos=(1.87e-14,1034,-3.446e-13) rot=(0,0,1;3.14159rad)
FEATURE [App::Link] Body002
  LinkPlacement = pos=(-2.8e-15,-18,18) rot=(1,0,0;4.71239rad)
  LinkedObject = -> <external 12_cross_beam.FCStd>#Body
  Placement = pos=(-2.8e-15,-18,18) rot=(1,0,0;4.71239rad)
FEATURE [App::FeaturePython] Joint  label="Distance"  # Assembly joint (typed FeaturePython)
  Activated = true
  AngleMax = 0
  AngleMin = 0
  Detach1 = false
  Detach2 = false
  Distance = 1
  Distance2 = 0
  EnableAngleMax = false
  EnableAngleMin = false
  EnableLengthMax = false
  EnableLengthMin = false
  JointType = 5 (Distance)
  LengthMax = 0
  LengthMin = 0
  Placement1 = pos=(1e-15,3.02549e-11,0) rot=(0,0,1;0rad)
  Placement2 = pos=(4.5e-15,-17,122.081) rot=(-1,0,0;1.5708rad)
  Reference1 = -> Assembly [Body002.Face7,Body002.Face7]
  Reference2 = -> Assembly [Body.Face3,Body.Vertex12]
FEATURE [App::FeaturePython] Joint001  label="Distance001"  # Assembly joint (typed FeaturePython)
  Activated = true
  AngleMax = 0
  AngleMin = 0
  Detach1 = false
  Detach2 = false
  Distance = 0
  Distance2 = 0
  EnableAngleMax = false
  EnableAngleMin = false
  EnableLengthMax = false
  EnableLengthMin = false
  JointType = 5 (Distance)
  LengthMax = 0
  LengthMin = 0
  Placement1 = pos=(17,1.172e-13,535) rot=(-0.57735,-0.57735,0.57735;2.0944rad)
  Placement2 = pos=(17,-6.5e-15,117.5) rot=(-0.57735,-0.57735,0.57735;2.0944rad)
  Reference1 = -> Assembly [Body002.Face10,Body002.Vertex10]
  Reference2 = -> Assembly [Body.Face10,Body.Face10]
FEATURE [App::FeaturePython] Joint002  label="Distance002"  # Assembly joint (typed FeaturePython)
  Activated = true
  AngleMax = 0
  AngleMin = 0
  Detach1 = false
  Detach2 = false
  Distance = -1
  Distance2 = 0
  EnableAngleMax = false
  EnableAngleMin = false
  EnableLengthMax = false
  EnableLengthMin = false
  JointType = 5 (Distance)
  LengthMax = 0
  LengthMin = 0
  Placement1 = pos=(-1e-15,17,535) rot=(0,-0.707107,0.707107;3.14159rad)
  Placement2 = pos=(11,-6.1e-15,0) rot=(0,0,1;0rad)
  Reference1 = -> Assembly [Body002.Face5,Body002.Vertex18]
  Reference2 = -> Assembly [Body.Face6,Body.Vertex14]
FEATURE [App::FeaturePython] Joint003  label="Distance003"  # Assembly joint (typed FeaturePython)
  Activated = true
  AngleMax = 0
  AngleMin = 0
  Detach1 = false
  Detach2 = false
  Distance = 1
  Distance2 = 0
  EnableAngleMax = false
  EnableAngleMin = false
  EnableLengthMax = false
  EnableLengthMin = false
  JointType = 5 (Distance)
  LengthMax = 0
  LengthMin = 0
  Placement1 = pos=(11,0,0) rot=(0,0,1;0rad)
  Placement2 = pos=(-1e-15,17,535) rot=(0,-0.707107,0.707107;3.14159rad)
  Reference1 = -> Assembly [Body001.Face6,Body001.Face6]
  Reference2 = -> Assembly [Body002.Face5,Body002.Vertex16]
FEATURE [App::FeaturePython] Joint004  label="Distance004"  # Assembly joint (typed FeaturePython)
  Activated = true
  AngleMax = 0
  AngleMin = 0
  Detach1 = false
  Detach2 = false
  Distance = 0
  Distance2 = 0
  EnableAngleMax = false
  EnableAngleMin = false
  EnableLengthMax = false
  EnableLengthMin = false
  JointType = 5 (Distance)
  LengthMax = 0
  LengthMin = 0
  Placement1 = pos=(17,0,117.5) rot=(0.57735,0.57735,-0.57735;4.18879rad)
  Placement2 = pos=(-17,1.172e-13,535) rot=(0.57735,-0.57735,0.57735;4.18879rad)
  Reference1 = -> Assembly [Body001.Face10,Body001.Vertex15]
  Reference2 = -> Assembly [Body002.Face1,Body002.Vertex4]
FEATURE [App::FeaturePython] Joint005  label="Distance005"  # Assembly joint (typed FeaturePython)
  Activated = true
  AngleMax = 0
  AngleMin = 0
  Detach1 = false
  Detach2 = false
  Distance = -1
  Distance2 = 0
  EnableAngleMax = false
  EnableAngleMin = false
  EnableLengthMax = false
  EnableLengthMin = false
  JointType = 5 (Distance)
  LengthMax = 0
  LengthMin = 0
  Placement1 = pos=(1e-15,3.04929e-11,1070) rot=(0,0,1;0rad)
  Placement2 = pos=(3.8e-15,-17,122.081) rot=(1,0,0;4.71239rad)
  Reference1 = -> Assembly [Body002.Face13,Body002.Vertex22]
  Reference2 = -> Assembly [Body001.Face3,Body001.Vertex11]
FEATURE [Assembly::JointGroup] Joints
  Group = -> [GroundedJoint,Joint,Joint001,Joint002,Joint003,Joint004,Joint005]
FEATURE [Assembly::AssemblyObject] Assembly
  Group = -> [Joints,Body,GroundedJoint,Body001,Body002,Joint,Joint001,Joint002,Joint003,Joint004,Joint005]
  Origin = -> Origin
  Type = Assembly
---- part 11_foot.FCStd = doc fcstd_6046575efeb6 ----
FCSTD DOCUMENT  (FreeCAD 1.0R39109 (Git))
Label: 02_foot
License: All rights reserved
LicenseURL: http://en.wikipedia.org/wiki/All_rights_reserved
objects: Sketcher::SketchObject×2, Spreadsheet::Sheet×1, PartDesign::Pad×1, PartDesign::Pocket×1, PartDesign::Body×1
note: 11 computed .brp shape members not serialized (recipe doc carries the construction recipe); baked Part::Feature solids carry a one-line shape summary decoded from their .brp

FEATURE [Sketcher::SketchObject] Sketch
  ArcFitTolerance = 1e-06
  AttachmentSupport = -> [XY_Plane]
  FullyConstrained = true
  MakeInternals = false
  MapMode = 5
  expr: Constraints[11] = Spreadsheet.width
  expr: Constraints[12] = Spreadsheet.height
  sketch-geometry (5):
    g0: LineSegment StartX=-17 StartY=17 StartZ=0 EndX=-17 EndY=-17 EndZ=0
    g1: LineSegment StartX=-17 StartY=-17 StartZ=0 EndX=17 EndY=-17 EndZ=0
    g2: LineSegment StartX=17 StartY=-17 StartZ=0 EndX=17 EndY=17 EndZ=0
    g3: LineSegment StartX=17 StartY=17 StartZ=0 EndX=-17 EndY=17 EndZ=0
    g4: LineSegment [constr] StartX=-17 StartY=17 StartZ=0 EndX=17 EndY=-17 EndZ=0
  constraints (13):
    c: Coincident(g0,g1)
    c: Coincident(g1,g2)
    c: Coincident(g2,g3)
    c: Coincident(g3,g0)
    c: Vertical(g0)
    c: Vertical(g2)
    c: Horizontal(g1)
    c: Horizontal(g3)
    c: Coincident(g4,g0)
    c: Coincident(g4,g1)
    c: Symmetric(g0,g1,g-1)
    c: DistanceX(g3,g3) = 34
    c: DistanceY(g0,g0) = 34
FEATURE [Spreadsheet::Sheet] Spreadsheet
  cells = A2='Breite; B2(width)=34; A3='Höhe; B3(height)=34; A4='Länge; B4(length)==width + 200 + 1; A5='Breite Schlitz; B5(widthmortise)=10; A6='Tiefe Schlitz; B6(depthmortise)=35
FEATURE [PartDesign::Pad] Pad
  Direction = (0,0,1)
  Length = 235
  Length2 = 10
  Profile = -> Sketch
  ReferenceAxis = -> Sketch [N_Axis]
  Suppressed = false
  Type = 0
  expr: Length = Spreadsheet.length
FEATURE [Sketcher::SketchObject] Sketch001
  ArcFitTolerance = 1e-06
  AttachmentSupport = -> [XY_Plane]
  FullyConstrained = true
  MakeInternals = false
  MapMode = 5
  expr: Constraints[10] = Spreadsheet.widthmortise
  expr: Constraints[11] = Spreadsheet.widthmortise / 2
  expr: Constraints[8] = Spreadsheet.width
  expr: Constraints[9] = Spreadsheet.width / 2
  sketch-geometry (4):
    g0: LineSegment StartX=-5 StartY=-17 StartZ=0 EndX=5 EndY=-17 EndZ=0
    g1: LineSegment StartX=5 StartY=-17 StartZ=0 EndX=5 EndY=17 EndZ=0
    g2: LineSegment StartX=5 StartY=17 StartZ=0 EndX=-5 EndY=17 EndZ=0
    g3: LineSegment StartX=-5 StartY=17 StartZ=0 EndX=-5 EndY=-17 EndZ=0
  constraints (12):
    c: Coincident(g0,g1)
    c: Coincident(g1,g2)
    c: Coincident(g2,g3)
    c: Coincident(g3,g0)
    c: Horizontal(g0)
    c: Horizontal(g2)
    c: Vertical(g1)
    c: Vertical(g3)
    c: DistanceY(g3,g3) = 34
    c: Distance(g-1,g2) = 17
    c: DistanceX(g2,g2) = 10
    c: Distance(g1,g-2) = 5
FEATURE [PartDesign::Pocket] Pocket
  BaseFeature = -> Pad
  Direction = (0,0,-1)
  Length = 35
  Length2 = 5
  Profile = -> Sketch001
  ReferenceAxis = -> Sketch001 [N_Axis]
  Reversed = true
  Suppressed = false
  Type = 0
  expr: Length = Spreadsheet.depthmortise
FEATURE [PartDesign::Body] Body
  AllowCompound = false
  Group = -> [Sketch,Pad,Sketch001,Pocket]
  Origin = -> Origin
  Tip = -> Pocket
---- part 12_cross_beam.FCStd = doc fcstd_1ac66e55c143 ----
FCSTD DOCUMENT  (FreeCAD 1.0R39109 (Git))
Label: 03_cross_beam
License: All rights reserved
LicenseURL: http://en.wikipedia.org/wiki/All_rights_reserved
objects: Sketcher::SketchObject×2, Spreadsheet::Sheet×1, PartDesign::Pad×1, PartDesign::Pocket×1, PartDesign::Plane×1, PartDesign::Mirrored×1, PartDesign::Body×1
note: 14 computed .brp shape members not serialized (recipe doc carries the construction recipe); baked Part::Feature solids carry a one-line shape summary decoded from their .brp

FEATURE [Spreadsheet::Sheet] Spreadsheet
  cells = A2='Breite; B2(width)=34; A3='Höhe; B3(height)=34; A4='Länge; B4(length)==2 * width + 1000 + 2; C4='Links und Rechts 1mm Überstand; A5='Breite Zapfen; B5(widthtenon)=12; A6='Tiefe Zapfen; B6(depthtenon)=35; A7='Breite Schlitz; B7(widthmortise)=10
FEATURE [Sketcher::SketchObject] Sketch
  ArcFitTolerance = 1e-06
  AttachmentSupport = -> [XY_Plane]
  FullyConstrained = true
  MakeInternals = false
  MapMode = 5
  expr: Constraints[11] = Spreadsheet.width
  expr: Constraints[12] = Spreadsheet.height
  sketch-geometry (5):
    g0: LineSegment StartX=-17 StartY=17 StartZ=0 EndX=-17 EndY=-17 EndZ=0
    g1: LineSegment StartX=-17 StartY=-17 StartZ=0 EndX=17 EndY=-17 EndZ=0
    g2: LineSegment StartX=17 StartY=-17 StartZ=0 EndX=17 EndY=17 EndZ=0
    g3: LineSegment StartX=17 StartY=17 StartZ=0 EndX=-17 EndY=17 EndZ=0
    g4: LineSegment [constr] StartX=-17 StartY=17 StartZ=0 EndX=17 EndY=-17 EndZ=0
  constraints (13):
    c: Coincident(g0,g1)
    c: Coincident(g1,g2)
    c: Coincident(g2,g3)
    c: Coincident(g3,g0)
    c: Vertical(g0)
    c: Vertical(g2)
    c: Horizontal(g1)
    c: Horizontal(g3)
    c: Coincident(g4,g0)
    c: Coincident(g4,g1)
    c: Symmetric(g0,g1,g-1)
    c: DistanceX(g3,g3) = 34
    c: DistanceY(g2,g2) = 34
FEATURE [PartDesign::Pad] Pad
  Direction = (0,0,1)
  Length = 1070
  Length2 = 10
  Profile = -> Sketch
  ReferenceAxis = -> Sketch [N_Axis]
  Suppressed = false
  Type = 0
  expr: Length = Spreadsheet.length
FEATURE [Sketcher::SketchObject] Sketch001
  ArcFitTolerance = 1e-06
  AttachmentSupport = -> [XY_Plane]
  FullyConstrained = true
  MakeInternals = false
  MapMode = 5
  expr: Constraints[16] = Spreadsheet.widthtenon
  expr: Constraints[18] = Spreadsheet.widthmortise
  expr: Constraints[19] = Spreadsheet.height
  expr: Constraints[24] = Spreadsheet.height / 2
  expr: Constraints[25] = Spreadsheet.width / 2
  sketch-geometry (9):
    g0: LineSegment StartX=-17 StartY=17 StartZ=0 EndX=-17 EndY=-17 EndZ=0
    g1: LineSegment StartX=-17 StartY=-17 StartZ=0 EndX=-5 EndY=-17 EndZ=0
    g2: LineSegment StartX=-5 StartY=-17 StartZ=0 EndX=-5 EndY=17 EndZ=0
    g3: LineSegment StartX=-5 StartY=17 StartZ=0 EndX=-17 EndY=17 EndZ=0
    g4: LineSegment StartX=17 StartY=-17 StartZ=0 EndX=17 EndY=17 EndZ=0
    g5: LineSegment StartX=17 StartY=17 StartZ=0 EndX=5 EndY=17 EndZ=0
    g6: LineSegment StartX=5 StartY=17 StartZ=0 EndX=5 EndY=-17 EndZ=0
    g7: LineSegment StartX=5 StartY=-17 StartZ=0 EndX=17 EndY=-17 EndZ=0
    g8: LineSegment [constr] StartX=-5 StartY=17 StartZ=0 EndX=5 EndY=17 EndZ=0
  constraints (26):
    c: Coincident(g0,g1)
    c: Coincident(g1,g2)
    c: Coincident(g2,g3)
    c: Coincident(g3,g0)
    c: Vertical(g0)
    c: Vertical(g2)
    c: Horizontal(g1)
    c: Horizontal(g3)
    c: Coincident(g4,g5)
    c: Coincident(g5,g6)
    c: Coincident(g6,g7)
    c: Coincident(g7,g4)
    c: Vertical(g4)
    c: Vertical(g6)
    c: Horizontal(g5)
    c: Horizontal(g7)
    c: DistanceX(g3,g3) = 12
    c: Equal(g3,g5)
    c: DistanceX(g2,g5) = 10
    c: DistanceY(g0,g0) = 34
    c: Equal(g0,g6)
    c: Coincident(g8,g2)
    c: Coincident(g8,g5)
    c: Horizontal(g8)
    c: Distance(g-1,g8) = 17
    c: Distance(g-2,g0) = 17
FEATURE [PartDesign::Pocket] Pocket
  BaseFeature = -> Pad
  Direction = (0,0,-1)
  Length = 35
  Length2 = 5
  Profile = -> Sketch001
  ReferenceAxis = -> Sketch001 [N_Axis]
  Reversed = true
  Suppressed = false
  Type = 0
  expr: Length = Spreadsheet.depthtenon
FEATURE [PartDesign::Plane] DatumPlane
  Length = 60
  MapMode = 2
  Placement = pos=(0,0,535) rot=(0,0,1;0rad)
  ResizeMode = 0
  Width = 60
  expr: .Placement.Base.z = Spreadsheet.length / 2
FEATURE [PartDesign::Mirrored] Mirrored
  BaseFeature = -> Pocket
  MirrorPlane = -> DatumPlane
  Originals = -> [Pocket]
  Suppressed = false
  TransformMode = 0
FEATURE [PartDesign::Body] Body
  AllowCompound = false
  Group = -> [Sketch,Pad,Sketch001,Pocket,DatumPlane,Mirrored]
  Origin = -> Origin
  Tip = -> Mirrored
